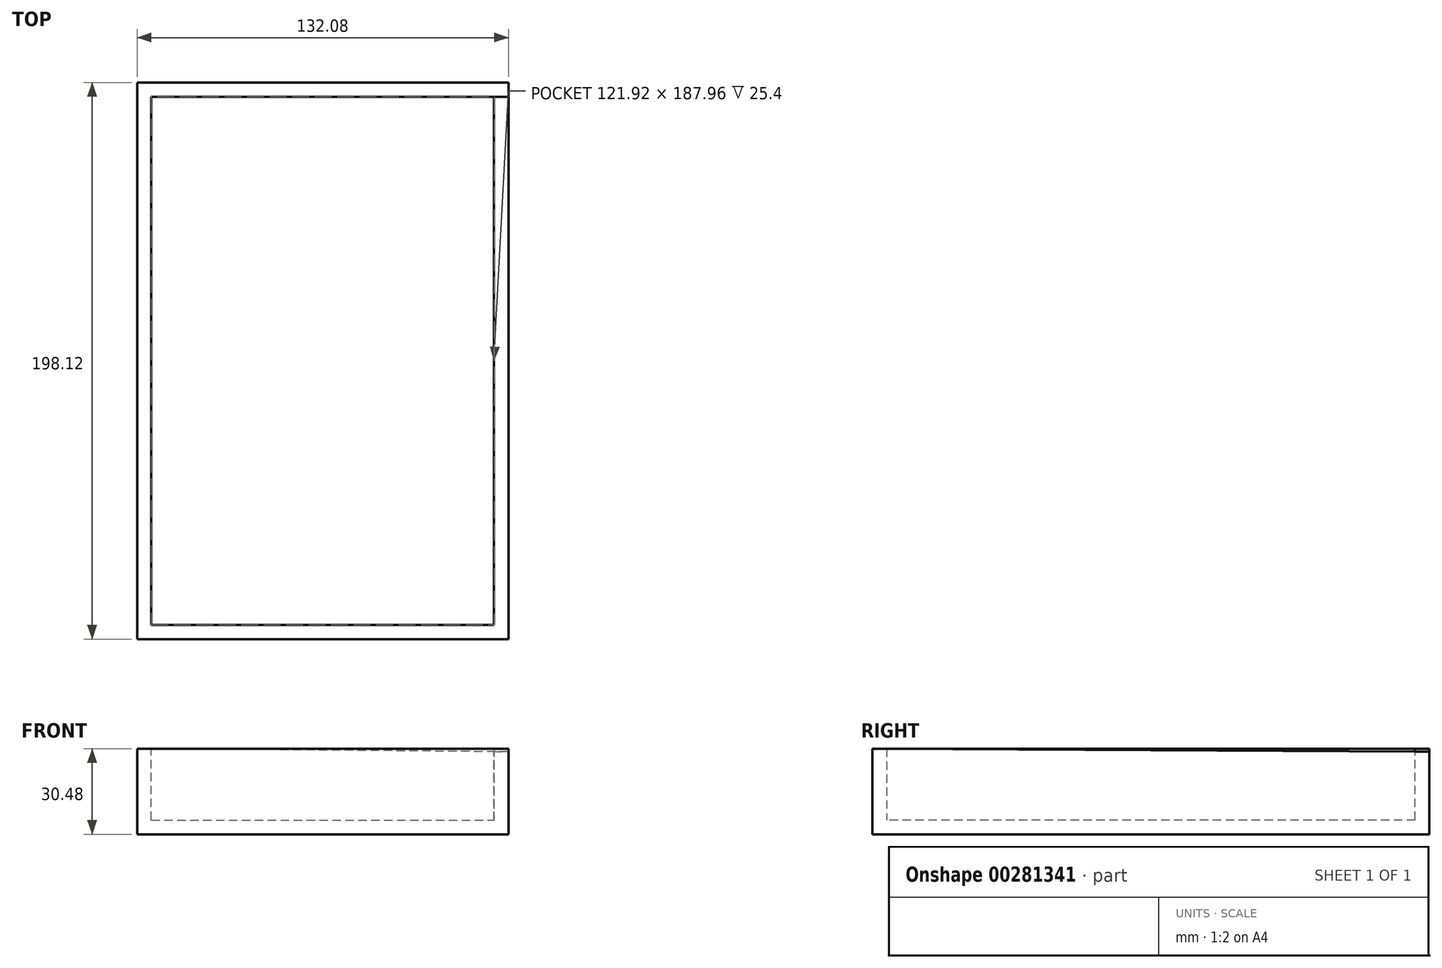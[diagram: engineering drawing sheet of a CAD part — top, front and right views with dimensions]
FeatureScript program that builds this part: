
annotation { "Feature Type Name" : "Feature", "Feature Type Description" : "" }
export const myFeature = defineFeature(function(context is Context, id is Id, definition is map)
    precondition{}
    {
        {
            var Q0;
            Q0=qCreatedBy(makeId("Top.planeOp"),FACE);
            var sketch = newSketch(context, id + "F0", { "sketchPlane" : qUnion([Q0])});
            skLineSegment(sketch, "E0.bottom", {"start": v(-76.2, 108.5) * mm, "end": v(55.88, 108.5) * mm});
            skLineSegment(sketch, "E0.top", {"start": v(-76.2, -89.62) * mm, "end": v(55.88, -89.62) * mm});
            skLineSegment(sketch, "E0.left", {"start": v(-76.2, 108.5) * mm, "end": v(-76.2, -89.62) * mm});
            skLineSegment(sketch, "E0.right", {"start": v(55.88, 108.5) * mm, "end": v(55.88, -89.62) * mm});
            skSolve(sketch);
        }
        {
            var Q0;
            Q0 = qSketchRegion(id + "F0", true);
            extrude(context, id + "F1", {"entities" : qUnion([Q0]), "depth" : 5.08 * mm});
        }
        {
            var Q0;
            Q0=makeQuery(id+"F1.opExtrude","SWEPT_FACE",FACE,{"disambiguationData":[OSD([sQuery(id+"F0.wireOp",EDGE,"E0.top")])]});
            var sketch = newSketch(context, id + "F2", { "sketchPlane" : qUnion([Q0])});
            skPoint(sketch, "E1", {"position": v(-166.26, 79.72) * mm});
            skLineSegment(sketch, "E2", {"start": v(-76.2, 5.08) * mm, "end": v(-76.2, 30.48) * mm});
            skLineSegment(sketch, "E3", {"start": v(-76.2, 30.48) * mm, "end": v(55.88, 30.48) * mm});
            skLineSegment(sketch, "E4", {"start": v(55.88, 30.48) * mm, "end": v(55.88, 5.08) * mm});
            skSolve(sketch);
        }
        {
            var Q0;
            Q0=makeQuery(id+"F2.imprint","IMPRINT",FACE,{"disambiguationData":[TD([[makeQuery(id+"F2.imprint","IMPRINT",EDGE,{"derivedFrom":sQuery(id+"F2.wireOp",EDGE,"E2")}),-1.0]])]});
            extrude(context, id + "F3", {"entities" : qUnion([Q0]), "operationType" : NewBodyOperationType.ADD, "oppositeDirection" : true, "depth" : 5.08 * mm});
        }
        {
            var Q0;
            Q0=makeQuery(id+"F3.boolean.opBoolean","MERGE",FACE,{"derivedFrom":[makeQuery(id+"F1.opExtrude","SWEPT_FACE",FACE,{"disambiguationData":[OSD([sQuery(id+"F0.wireOp",EDGE,"E0.left")])]}),makeQuery(id+"F3.opExtrude","SWEPT_FACE",FACE,{"disambiguationData":[OSD([sQuery(id+"F2.wireOp",EDGE,"E2")])]})]});
            var sketch = newSketch(context, id + "F4", { "sketchPlane" : qUnion([Q0])});
            skLineSegment(sketch, "E5", {"start": v(-108.5, 5.08) * mm, "end": v(-108.5, 30.48) * mm});
            skLineSegment(sketch, "E6", {"start": v(-108.5, 30.48) * mm, "end": v(84.54, 30.48) * mm});
            skLineSegment(sketch, "E7.0", {"start": v(-108.5, 5.08) * mm, "end": v(84.54, 5.08) * mm});
            skSolve(sketch);
        }
        {
            var Q0;
            Q0=makeQuery(id+"F4.imprint","IMPRINT",FACE,{"disambiguationData":[TD([[makeQuery(id+"F4.imprint","IMPRINT",EDGE,{"derivedFrom":sQuery(id+"F4.wireOp",EDGE,"E5")}),-1.0]])]});
            extrude(context, id + "F5", {"entities" : qUnion([Q0]), "operationType" : NewBodyOperationType.ADD, "oppositeDirection" : true, "depth" : 5.08 * mm});
        }
        {
            var Q0;
            Q0=makeQuery(id+"F5.boolean.opBoolean","MERGE",FACE,{"derivedFrom":[makeQuery(id+"F1.opExtrude","SWEPT_FACE",FACE,{"disambiguationData":[OSD([sQuery(id+"F0.wireOp",EDGE,"E0.bottom")])]}),makeQuery(id+"F5.opExtrude","SWEPT_FACE",FACE,{"disambiguationData":[OSD([sQuery(id+"F4.wireOp",EDGE,"E5")])]})]});
            var sketch = newSketch(context, id + "F6", { "sketchPlane" : qUnion([Q0])});
            skLineSegment(sketch, "E8", {"start": v(-55.88, 5.08) * mm, "end": v(-55.88, 29.36) * mm});
            skLineSegment(sketch, "E9", {"start": v(-55.88, 29.36) * mm, "end": v(71.12, 30.48) * mm});
            skSolve(sketch);
        }
        {
            var Q0;
            Q0=makeQuery(id+"F6.imprint","IMPRINT",FACE,{"disambiguationData":[TD([[makeQuery(id+"F6.imprint","IMPRINT",EDGE,{"derivedFrom":sQuery(id+"F6.wireOp",EDGE,"E8")}),-1.0]])]});
            extrude(context, id + "F7", {"entities" : qUnion([Q0]), "operationType" : NewBodyOperationType.ADD, "oppositeDirection" : true, "depth" : 5.08 * mm});
        }
        {
            var Q0;
            Q0=makeQuery(id+"F7.boolean.opBoolean","MERGE",FACE,{"derivedFrom":[makeQuery(id+"F3.boolean.opBoolean","MERGE",FACE,{"derivedFrom":[makeQuery(id+"F1.opExtrude","SWEPT_FACE",FACE,{"disambiguationData":[OSD([sQuery(id+"F0.wireOp",EDGE,"E0.right")])]}),makeQuery(id+"F3.opExtrude","SWEPT_FACE",FACE,{"disambiguationData":[OSD([sQuery(id+"F2.wireOp",EDGE,"E4")])]})]}),makeQuery(id+"F7.opExtrude","SWEPT_FACE",FACE,{"disambiguationData":[OSD([sQuery(id+"F6.wireOp",EDGE,"E8")])]})]});
            var sketch = newSketch(context, id + "F8", { "sketchPlane" : qUnion([Q0])});
            skLineSegment(sketch, "E10", {"start": v(-84.54, 30.48) * mm, "end": v(103.42, 29.36) * mm});
            skSolve(sketch);
        }
        {
            var Q0;
            Q0=makeQuery(id+"F8.imprint","IMPRINT",FACE,{"disambiguationData":[TD([[makeQuery(id+"F8.imprint","IMPRINT",EDGE,{"derivedFrom":sQuery(id+"F8.wireOp",EDGE,"E10")}),-1.0]])]});
            extrude(context, id + "F9", {"entities" : qUnion([Q0]), "operationType" : NewBodyOperationType.ADD, "oppositeDirection" : true, "depth" : 5.08 * mm});
        }
    });
